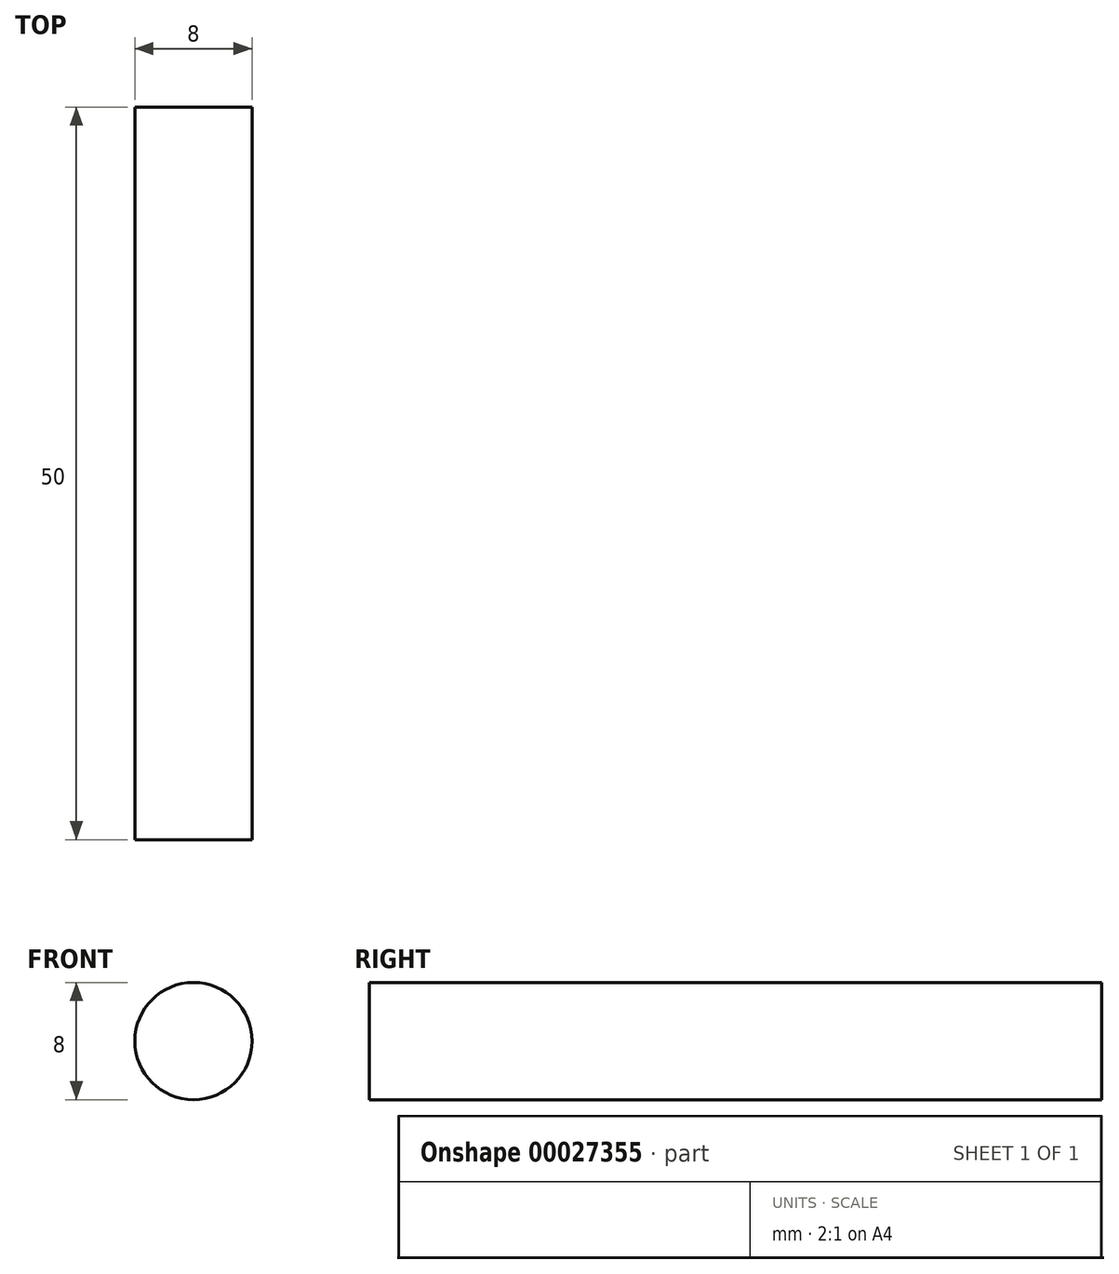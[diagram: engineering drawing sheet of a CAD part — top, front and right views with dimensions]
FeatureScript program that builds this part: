
annotation { "Feature Type Name" : "Feature", "Feature Type Description" : "" }
export const myFeature = defineFeature(function(context is Context, id is Id, definition is map)
    precondition{}
    {
        {
            var Q0;
            Q0=qCreatedBy(makeId("Front.planeOp"),FACE);
            var sketch = newSketch(context, id + "F0", { "sketchPlane" : qUnion([Q0])});
            skCircle(sketch, "E0", {"center": v(0, 0) * mm, "radius": 4 * mm});
            skSolve(sketch);
        }
        {
            var Q0;
            Q0=makeQuery(id+"F0.imprint","IMPRINT",FACE,{"disambiguationData":[TD([[makeQuery(id+"F0.imprint","IMPRINT",EDGE,{"derivedFrom":sQuery(id+"F0.wireOp",EDGE,"E0")}),1.0]])]});
            extrude(context, id + "F1", {"entities" : qUnion([Q0]), "depth" : 50 * mm});
        }
    });
